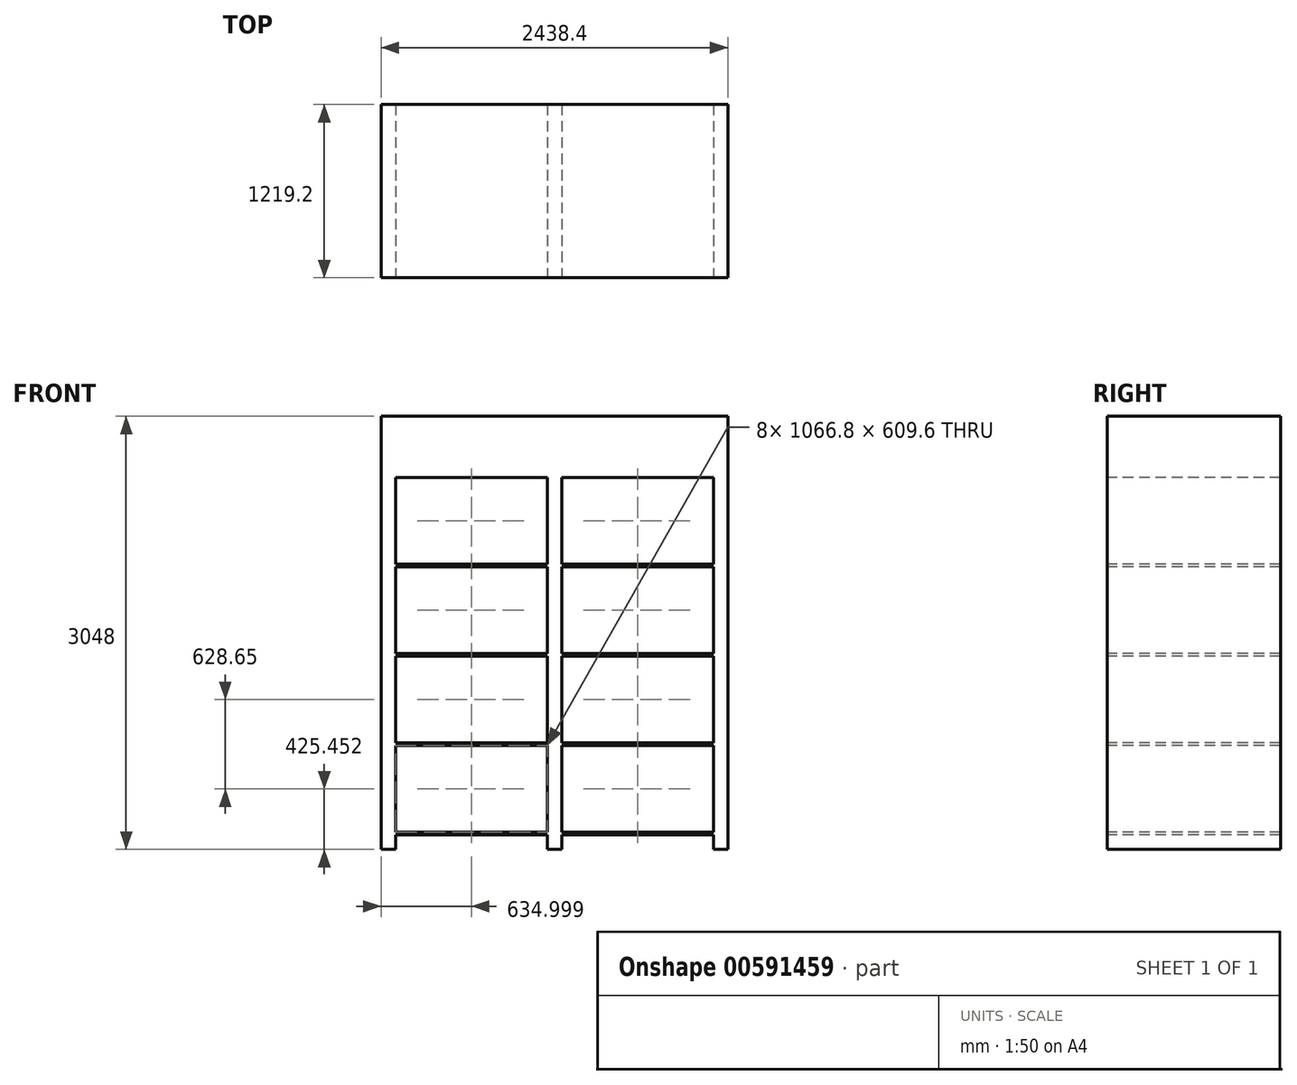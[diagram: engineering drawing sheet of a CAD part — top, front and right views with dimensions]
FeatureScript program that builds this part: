
annotation { "Feature Type Name" : "Feature", "Feature Type Description" : "" }
export const myFeature = defineFeature(function(context is Context, id is Id, definition is map)
    precondition{}
    {
        {
            var Q0;
            Q0=qCreatedBy(makeId("Front.planeOp"),FACE);
            var sketch = newSketch(context, id + "F0", { "sketchPlane" : qUnion([Q0])});
            skLineSegment(sketch, "E0.bottom", {"start": v(-1217.5, 1712.82) * mm, "end": v(1220.9, 1712.82) * mm});
            skLineSegment(sketch, "E0.top", {"start": v(-1217.5, -1335.18) * mm, "end": v(1220.9, -1335.18) * mm});
            skLineSegment(sketch, "E0.left", {"start": v(-1217.5, 1712.82) * mm, "end": v(-1217.5, -1335.18) * mm});
            skLineSegment(sketch, "E0.right", {"start": v(1220.9, 1712.82) * mm, "end": v(1220.9, -1335.18) * mm});
            skSolve(sketch);
        }
        {
            var Q0;
            Q0=makeQuery(id+"F0.imprint","IMPRINT",FACE,{"disambiguationData":[TD([[makeQuery(id+"F0.imprint","IMPRINT",EDGE,{"derivedFrom":sQuery(id+"F0.wireOp",EDGE,"E0.bottom")}),-1.0]])]});
            extrude(context, id + "F1", {"entities" : qUnion([Q0]), "depth" : 1219.2 * mm, "offsetDistance" : 25.4 * mm});
        }
        {
            var Q0;
            Q0=makeQuery(id+"F1.opExtrude","CAP_FACE",FACE,{"disambiguationData":[OSD([sQuery(id+"F0.wireOp",EDGE,"E0.bottom"),sQuery(id+"F0.wireOp",EDGE,"E0.top"),sQuery(id+"F0.wireOp",EDGE,"E0.left"),sQuery(id+"F0.wireOp",EDGE,"E0.right")])],"isStart":false});
            var sketch = newSketch(context, id + "F2", { "sketchPlane" : qUnion([Q0])});
            skLineSegment(sketch, "E1.bottom", {"start": v(-1115.9, -1214.53) * mm, "end": v(-49.1, -1214.53) * mm});
            skLineSegment(sketch, "E1.top", {"start": v(-1115.9, -604.93) * mm, "end": v(-49.1, -604.93) * mm});
            skLineSegment(sketch, "E1.left", {"start": v(-1115.9, -1214.53) * mm, "end": v(-1115.9, -604.93) * mm});
            skLineSegment(sketch, "E1.right", {"start": v(1119.3, -1214.53) * mm, "end": v(1119.3, -604.93) * mm});
            skLineSegment(sketch, "E2.left", {"start": v(-49.1, -604.93) * mm, "end": v(-49.1, -1214.53) * mm});
            skLineSegment(sketch, "E2.right", {"start": v(52.5, -604.93) * mm, "end": v(52.5, -1214.53) * mm});
            skLineSegment(sketch, "E3.trimOffspring", {"start": v(52.5, -604.93) * mm, "end": v(1119.3, -604.93) * mm});
            skLineSegment(sketch, "E4.trimOffspring", {"start": v(52.5, -1214.53) * mm, "end": v(1119.3, -1214.53) * mm});
            skPoint(sketch, "E5.oppositeSnap0", {"position": v(-49.1, -909.73) * mm});
            skLineSegment(sketch, "E5.bottom", {"start": v(-1115.9, -585.88) * mm, "end": v(-49.1, -585.88) * mm});
            skLineSegment(sketch, "E5.top", {"start": v(-1115.9, 23.72) * mm, "end": v(-49.1, 23.72) * mm});
            skLineSegment(sketch, "E5.left", {"start": v(-1115.9, -585.88) * mm, "end": v(-1115.9, 23.72) * mm});
            skLineSegment(sketch, "E5.right", {"start": v(-49.1, -585.88) * mm, "end": v(-49.1, 23.72) * mm});
            skLineSegment(sketch, "E6.bottom", {"start": v(52.5, -585.88) * mm, "end": v(1119.3, -585.88) * mm});
            skLineSegment(sketch, "E6.top", {"start": v(52.5, 23.72) * mm, "end": v(1119.3, 23.72) * mm});
            skLineSegment(sketch, "E6.left", {"start": v(52.5, -585.88) * mm, "end": v(52.5, 23.72) * mm});
            skLineSegment(sketch, "E6.right", {"start": v(1119.3, -585.88) * mm, "end": v(1119.3, 23.72) * mm});
            skLineSegment(sketch, "E7.bottom", {"start": v(-1115.9, 42.77) * mm, "end": v(-49.1, 42.77) * mm});
            skLineSegment(sketch, "E7.top", {"start": v(-1115.9, 652.37) * mm, "end": v(-49.1, 652.37) * mm});
            skLineSegment(sketch, "E7.left", {"start": v(-1115.9, 42.77) * mm, "end": v(-1115.9, 652.37) * mm});
            skLineSegment(sketch, "E7.right", {"start": v(-49.1, 42.77) * mm, "end": v(-49.1, 652.37) * mm});
            skPoint(sketch, "E8.oppositeSnap0", {"position": v(-582.5, 652.37) * mm});
            skLineSegment(sketch, "E8.bottom", {"start": v(52.5, 42.77) * mm, "end": v(1119.3, 42.77) * mm});
            skLineSegment(sketch, "E8.top", {"start": v(52.5, 652.37) * mm, "end": v(1119.3, 652.37) * mm});
            skLineSegment(sketch, "E8.left", {"start": v(52.5, 42.77) * mm, "end": v(52.5, 652.37) * mm});
            skLineSegment(sketch, "E8.right", {"start": v(1119.3, 42.77) * mm, "end": v(1119.3, 652.37) * mm});
            skLineSegment(sketch, "E9.bottom", {"start": v(-1115.9, 671.42) * mm, "end": v(-49.1, 671.42) * mm});
            skLineSegment(sketch, "E9.top", {"start": v(-1115.9, 1281.02) * mm, "end": v(-49.1, 1281.02) * mm});
            skLineSegment(sketch, "E9.left", {"start": v(-1115.9, 671.42) * mm, "end": v(-1115.9, 1281.02) * mm});
            skLineSegment(sketch, "E9.right", {"start": v(-49.1, 671.42) * mm, "end": v(-49.1, 1281.02) * mm});
            skLineSegment(sketch, "E10.bottom", {"start": v(52.5, 671.42) * mm, "end": v(1119.3, 671.42) * mm});
            skLineSegment(sketch, "E10.top", {"start": v(52.5, 1281.02) * mm, "end": v(1119.3, 1281.02) * mm});
            skLineSegment(sketch, "E10.left", {"start": v(52.5, 671.42) * mm, "end": v(52.5, 1281.02) * mm});
            skLineSegment(sketch, "E10.right", {"start": v(1119.3, 671.42) * mm, "end": v(1119.3, 1281.02) * mm});
            skLineSegment(sketch, "E11.bottom", {"start": v(-1115.9, -1335.18) * mm, "end": v(-49.1, -1335.18) * mm});
            skLineSegment(sketch, "E11.top", {"start": v(-1115.9, -1233.58) * mm, "end": v(-49.1, -1233.58) * mm});
            skLineSegment(sketch, "E11.left", {"start": v(-1115.9, -1335.18) * mm, "end": v(-1115.9, -1233.58) * mm});
            skLineSegment(sketch, "E11.right", {"start": v(-49.1, -1335.18) * mm, "end": v(-49.1, -1233.58) * mm});
            skLineSegment(sketch, "E12.bottom", {"start": v(52.5, -1335.18) * mm, "end": v(1119.3, -1335.18) * mm});
            skLineSegment(sketch, "E12.top", {"start": v(52.5, -1233.58) * mm, "end": v(1119.3, -1233.58) * mm});
            skLineSegment(sketch, "E12.left", {"start": v(52.5, -1335.18) * mm, "end": v(52.5, -1233.58) * mm});
            skLineSegment(sketch, "E12.right", {"start": v(1119.3, -1335.18) * mm, "end": v(1119.3, -1233.58) * mm});
            skLineSegment(sketch, "E13.bottom", {"start": v(-1719.93, 1933.83) * mm, "end": v(1729.34, 1933.83) * mm});
            skLineSegment(sketch, "E13.top", {"start": v(-1719.93, -1744.12) * mm, "end": v(1729.34, -1744.12) * mm});
            skLineSegment(sketch, "E13.left", {"start": v(-1719.93, 1933.83) * mm, "end": v(-1719.93, -1744.12) * mm});
            skLineSegment(sketch, "E13.right", {"start": v(1729.34, 1933.83) * mm, "end": v(1729.34, -1744.12) * mm});
            skSolve(sketch);
        }
        {
            var Q0;
            {var subQ2=sQuery(id+"F2.wireOp",EDGE,"E11.bottom");Q0=makeQuery(id+"F2.imprint","IMPRINT",FACE,{"disambiguationData":[TD([[makeQuery(id+"F2.imprint","IMPRINT",EDGE,{"derivedFrom":subQ2}),-1.0]])]});}
            var Q1;
            Q1=makeQuery(id+"F2.imprint","IMPRINT",FACE,{"disambiguationData":[TD([[makeQuery(id+"F2.imprint","IMPRINT",EDGE,{"derivedFrom":sQuery(id+"F2.wireOp",EDGE,"E9.bottom")}),1.0]])]});
            var Q2;
            Q2=makeQuery(id+"F2.imprint","IMPRINT",FACE,{"disambiguationData":[TD([[makeQuery(id+"F2.imprint","IMPRINT",EDGE,{"derivedFrom":sQuery(id+"F2.wireOp",EDGE,"E7.bottom")}),1.0]])]});
            var Q3;
            Q3=makeQuery(id+"F2.imprint","IMPRINT",FACE,{"disambiguationData":[TD([[makeQuery(id+"F2.imprint","IMPRINT",EDGE,{"derivedFrom":sQuery(id+"F2.wireOp",EDGE,"E8.bottom")}),1.0]])]});
            var Q4;
            Q4=makeQuery(id+"F2.imprint","IMPRINT",FACE,{"disambiguationData":[TD([[makeQuery(id+"F2.imprint","IMPRINT",EDGE,{"derivedFrom":sQuery(id+"F2.wireOp",EDGE,"E10.bottom")}),1.0]])]});
            var Q5;
            Q5=makeQuery(id+"F2.imprint","IMPRINT",FACE,{"disambiguationData":[TD([[makeQuery(id+"F2.imprint","IMPRINT",EDGE,{"derivedFrom":sQuery(id+"F2.wireOp",EDGE,"E6.bottom")}),1.0]])]});
            var Q6;
            Q6=makeQuery(id+"F2.imprint","IMPRINT",FACE,{"disambiguationData":[TD([[makeQuery(id+"F2.imprint","IMPRINT",EDGE,{"derivedFrom":sQuery(id+"F2.wireOp",EDGE,"E1.right")}),1.0]])]});
            var Q7;
            Q7=makeQuery(id+"F2.imprint","IMPRINT",FACE,{"disambiguationData":[TD([[makeQuery(id+"F2.imprint","IMPRINT",EDGE,{"derivedFrom":sQuery(id+"F2.wireOp",EDGE,"E1.bottom")}),1.0]])]});
            var Q8;
            Q8=makeQuery(id+"F2.imprint","IMPRINT",FACE,{"disambiguationData":[TD([[makeQuery(id+"F2.imprint","IMPRINT",EDGE,{"derivedFrom":sQuery(id+"F2.wireOp",EDGE,"E5.bottom")}),1.0]])]});
            var Q9;
            Q9=makeQuery(id+"F2.imprint","IMPRINT",FACE,{"disambiguationData":[TD([[makeQuery(id+"F2.imprint","IMPRINT",EDGE,{"derivedFrom":sQuery(id+"F2.wireOp",EDGE,"E11.bottom")}),1.0]])]});
            var Q10;
            Q10=makeQuery(id+"F2.imprint","IMPRINT",FACE,{"disambiguationData":[TD([[makeQuery(id+"F2.imprint","IMPRINT",EDGE,{"derivedFrom":sQuery(id+"F2.wireOp",EDGE,"E12.bottom")}),1.0]])]});
            extrude(context, id + "F3", {"entities" : qUnion([Q0, Q1, Q2, Q3, Q4, Q5, Q6, Q7, Q8, Q9, Q10]), "operationType" : NewBodyOperationType.REMOVE, "endBound" : BoundingType.THROUGH_ALL, "oppositeDirection" : true, "depth" : 25.4 * mm, "offsetDistance" : 25.4 * mm});
        }
    });
